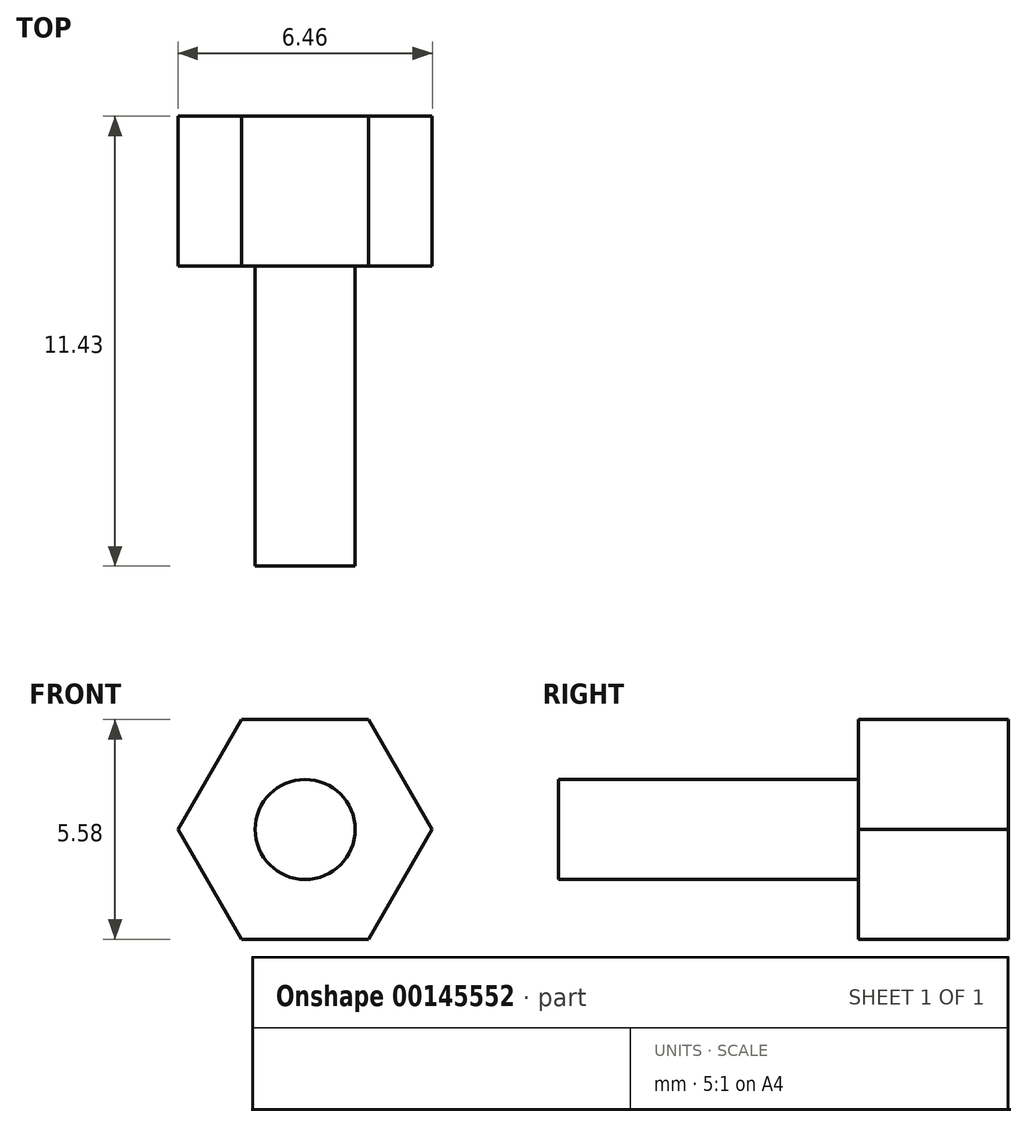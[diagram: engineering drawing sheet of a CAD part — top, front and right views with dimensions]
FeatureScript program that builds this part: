
annotation { "Feature Type Name" : "Feature", "Feature Type Description" : "" }
export const myFeature = defineFeature(function(context is Context, id is Id, definition is map)
    precondition{}
    {
        {
            var Q0;
            Q0=qCreatedBy(makeId("Front.planeOp"),FACE);
            var sketch = newSketch(context, id + "F0", { "sketchPlane" : qUnion([Q0])});
            skCircle(sketch, "E0.cCircle", {"center": v(0, 0) * mm, "radius": 2.8 * mm, "construction": true});
            skLineSegment(sketch, "E0.0", {"start": v(1.61, 2.8) * mm, "end": v(3.23, 0) * mm});
            skLineSegment(sketch, "E0.1", {"start": v(3.23, 0) * mm, "end": v(1.61, -2.8) * mm});
            skLineSegment(sketch, "E0.2", {"start": v(1.61, -2.8) * mm, "end": v(-1.61, -2.8) * mm});
            skLineSegment(sketch, "E0.3", {"start": v(-1.61, -2.8) * mm, "end": v(-3.23, 0) * mm});
            skLineSegment(sketch, "E0.4", {"start": v(-3.23, 0) * mm, "end": v(-1.61, 2.8) * mm});
            skLineSegment(sketch, "E0.5", {"start": v(-1.61, 2.8) * mm, "end": v(1.61, 2.8) * mm});
            skPoint(sketch, "E0.0.midPoint", {"position": v(2.42, 1.4) * mm});
            skSolve(sketch);
        }
        {
            var Q0;
            Q0 = qSketchRegion(id + "F0", true);
            extrude(context, id + "F1", {"entities" : qUnion([Q0]), "depth" : 3.8 * mm});
        }
        {
            var Q0;
            Q0=makeQuery(id+"F1.opExtrude","CAP_FACE",FACE,{"disambiguationData":[OSD([sQuery(id+"F0.wireOp",EDGE,"E0.0"),sQuery(id+"F0.wireOp",EDGE,"E0.1"),sQuery(id+"F0.wireOp",EDGE,"E0.2"),sQuery(id+"F0.wireOp",EDGE,"E0.3"),sQuery(id+"F0.wireOp",EDGE,"E0.4"),sQuery(id+"F0.wireOp",EDGE,"E0.5")])],"isStart":false});
            var sketch = newSketch(context, id + "F2", { "sketchPlane" : qUnion([Q0])});
            skCircle(sketch, "E1", {"center": v(0, 0) * mm, "radius": 1.27 * mm});
            skSolve(sketch);
        }
        {
            var Q0;
            Q0 = qSketchRegion(id + "F2", true);
            extrude(context, id + "F3", {"entities" : qUnion([Q0]), "operationType" : NewBodyOperationType.ADD, "depth" : 7.62 * mm});
        }
    });
